# Revit family: Haworth_BeHold_Accessory_PedestalShelf
name_source: partatom
category: Furniture Systems
revit_build: Autodesk Revit 2018 (Build: 20170223_1515(x64)
units: mm (PartAtom-declared; Revit-internal decimal feet)

## family parameters
Always vertical = Yes
Cut with Voids When Loaded = No
OmniClass Number = 23.40.70.14.64.21
OmniClass Title = Systems Furniture
Part Type = Normal
Room Calculation Point = No
Round Connector Dimension = Use Diameter
Shared = No
Work Plane-Based = No

## types (3) — shared parameters
Actual Height = 1/2"
Actual Width = 12"
Assembly Code = E2020200
Custom Size = No
Description = Haworth - Be_Hold - Accessory - Pedestal Shelf
Manufacturer = Haworth
Max. Depth = 30"
Max. Width = 12"
Min. Depth = 18"
Min. Width = 12"
Model = Haworth Be_Hold
Revision Number = 1
Size = Verify Final Dim. w/ Haworth
Standard Depths = 18, 24, 30 in.
Sustainability Info = https://www.haworth.com
Trim Finish = Haworth _ Paint _ Sky Blue
Warranty = http://www.haworth.com

## per-type parameters (varying)
| type | Actual Depth | Depth | URL | URL - Product |
| 30d | 30" | 30" | http://www.haworth.com | http://www.haworth.com |
| 24d | 24" | 24" | www.haworth.com |  |
| 18d | 18" | 18" | www.haworth.com |  |

## geometry (parser evidence)
native form markers: Sweep x3
no freeform markers — native parametric forms only
